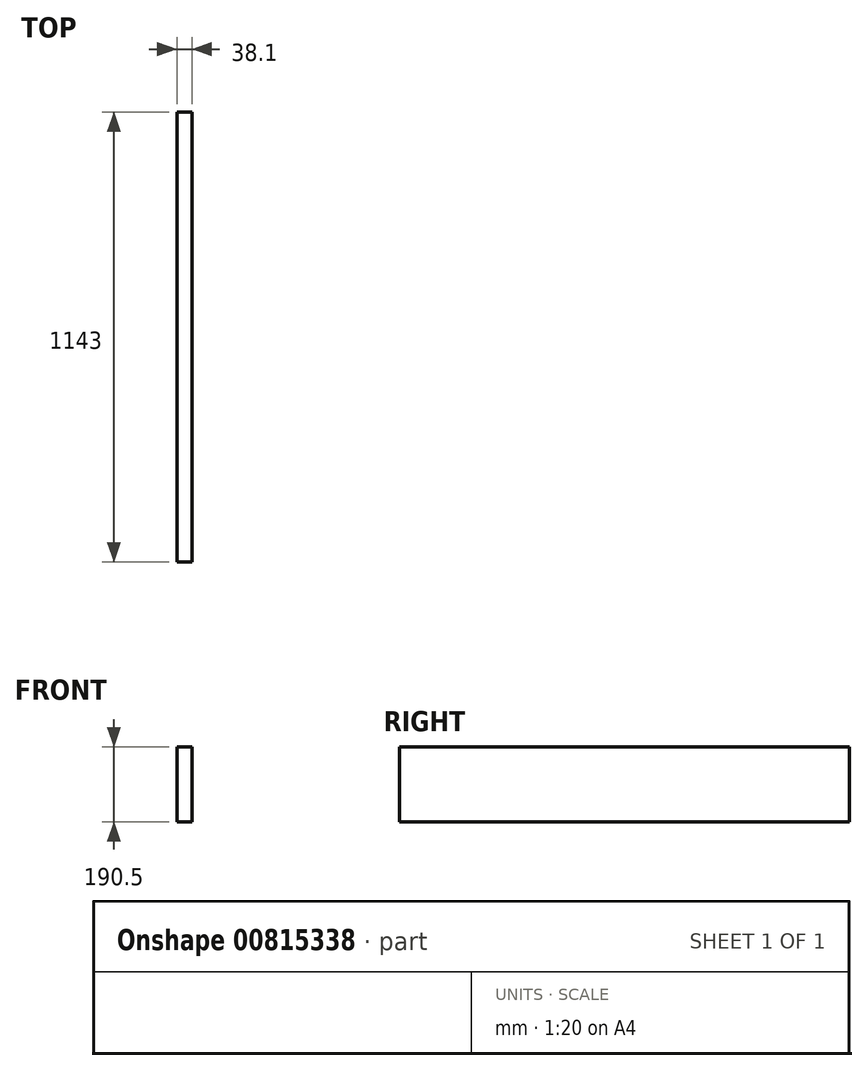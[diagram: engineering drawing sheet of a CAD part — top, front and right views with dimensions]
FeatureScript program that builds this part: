
annotation { "Feature Type Name" : "Feature", "Feature Type Description" : "" }
export const myFeature = defineFeature(function(context is Context, id is Id, definition is map)
    precondition{}
    {
        {
            var Q0;
            Q0=qCreatedBy(makeId("Front.planeOp"),FACE);
            var sketch = newSketch(context, id + "F0", { "sketchPlane" : qUnion([Q0])});
            skLineSegment(sketch, "E0.bottom", {"start": v(-19.05, 95.25) * mm, "end": v(19.05, 95.25) * mm});
            skLineSegment(sketch, "E0.top", {"start": v(-19.05, -95.25) * mm, "end": v(19.05, -95.25) * mm});
            skLineSegment(sketch, "E0.left", {"start": v(-19.05, 95.25) * mm, "end": v(-19.05, -95.25) * mm});
            skLineSegment(sketch, "E0.right", {"start": v(19.05, 95.25) * mm, "end": v(19.05, -95.25) * mm});
            skSolve(sketch);
        }
        {
            var Q0;
            Q0=qSketchRegion(id+"F0",true);
            extrude(context, id + "F1", {"entities" : qUnion([Q0]), "endBound" : BoundingType.SYMMETRIC, "depth" : 1143 * mm, "offsetDistance" : 25.4 * mm});
        }
    });
